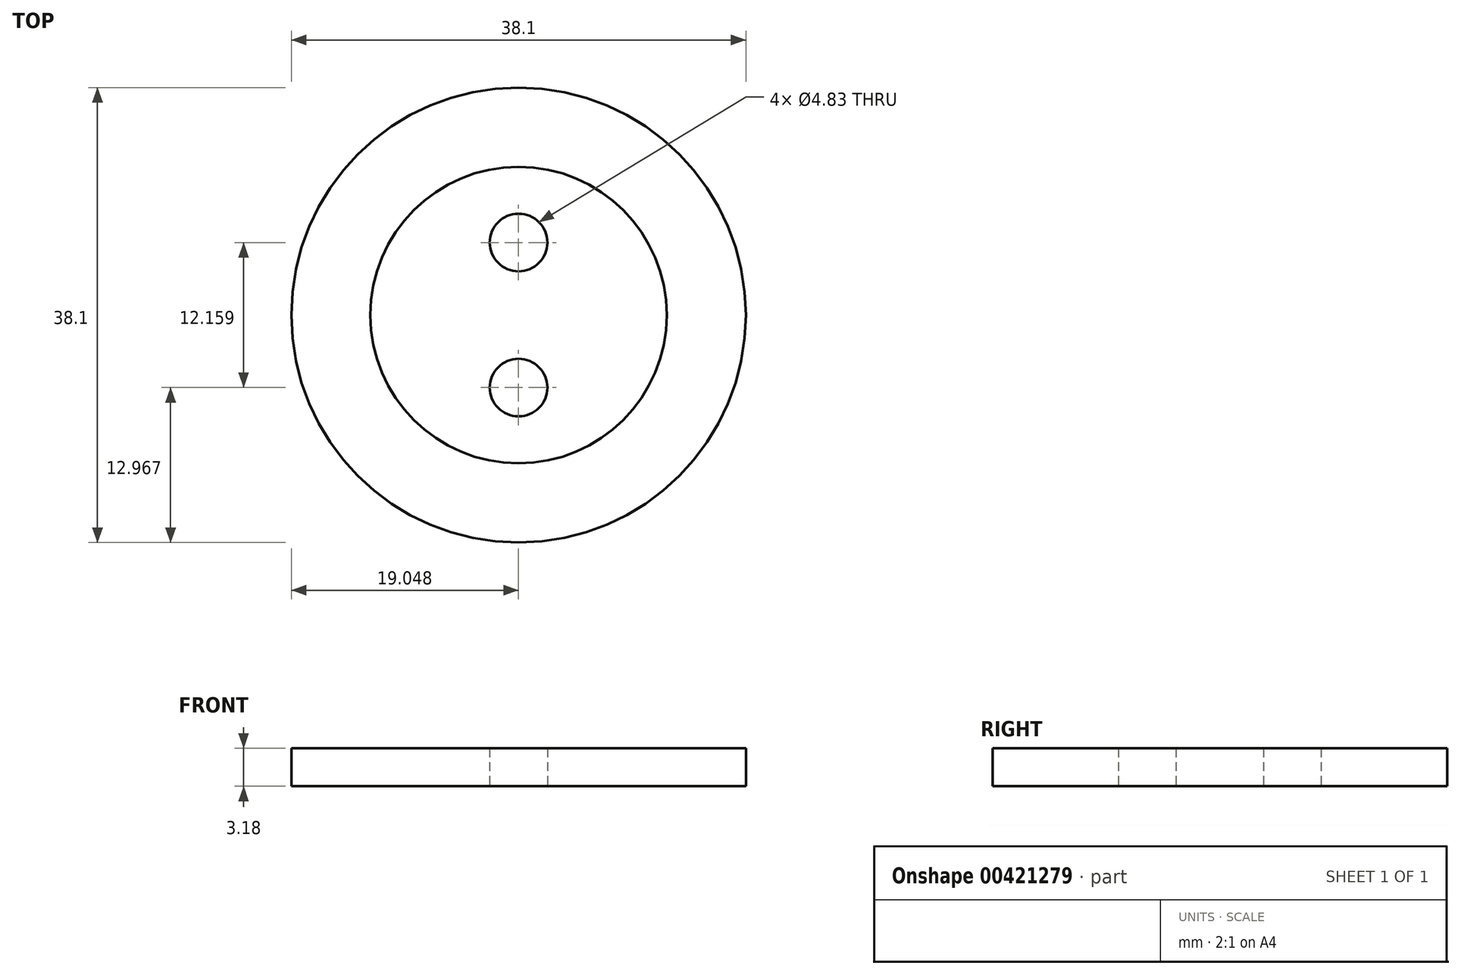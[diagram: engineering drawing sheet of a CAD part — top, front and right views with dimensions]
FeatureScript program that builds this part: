
annotation { "Feature Type Name" : "Feature", "Feature Type Description" : "" }
export const myFeature = defineFeature(function(context is Context, id is Id, definition is map)
    precondition{}
    {
        {
            assignVariable(context, id + "F0", {"name" : "flange_thickness", "anyValue" : 3.17 * mm});
        }
        {
            var Q0;
            Q0=qCreatedBy(makeId("Top.planeOp"),FACE);
            var sketch = newSketch(context, id + "F1", { "sketchPlane" : qUnion([Q0])});
            skCircle(sketch, "E0", {"center": v(-45.4, 36.92) * mm, "radius": 19.05 * mm});
            skCircle(sketch, "E1", {"center": v(-45.4, 36.92) * mm, "radius": 6.08 * mm, "construction": true});
            skCircle(sketch, "E2", {"center": v(-45.4, 43) * mm, "radius": 2.41 * mm});
            skCircle(sketch, "E3", {"center": v(-45.4, 30.84) * mm, "radius": 2.41 * mm});
            skSolve(sketch);
        }
        {
            var Q0;
            Q0=makeQuery(id+"F1.imprint","IMPRINT",FACE,{"disambiguationData":[TD([[makeQuery(id+"F1.imprint","IMPRINT",EDGE,{"derivedFrom":sQuery(id+"F1.wireOp",EDGE,"E0")}),1.0]])]});
            extrude(context, id + "F2", {"entities" : qUnion([Q0]), "depth" : getVariable(context, 'flange_thickness')});
        }
        {
            var Q0;
            Q0=makeQuery(id+"F2.opExtrude","CAP_FACE",FACE,{"disambiguationData":[OSD([sQuery(id+"F1.wireOp",EDGE,"E0"),sQuery(id+"F1.wireOp",EDGE,"E2"),sQuery(id+"F1.wireOp",EDGE,"E3")])],"isStart":false});
            var sketch = newSketch(context, id + "F3", { "sketchPlane" : qUnion([Q0])});
            skCircle(sketch, "E4.0.0", {"center": v(-45.4, 36.92) * mm, "radius": 19.05 * mm});
            skCircle(sketch, "E5", {"center": v(-45.4, 36.92) * mm, "radius": 12.42 * mm});
            skCircle(sketch, "E6.0", {"center": v(-45.4, 43) * mm, "radius": 2.41 * mm});
            skCircle(sketch, "E7.0", {"center": v(-45.4, 30.84) * mm, "radius": 2.41 * mm});
            skSolve(sketch);
        }
        {
            var Q0;
            Q0=makeQuery(id+"F3.imprint","IMPRINT",FACE,{"disambiguationData":[TD([[makeQuery(id+"F3.imprint","IMPRINT",EDGE,{"derivedFrom":sQuery(id+"F3.wireOp",EDGE,"E5")}),1.0]])]});
            extrude(context, id + "F4", {"entities" : qUnion([Q0]), "depth" : 1 / 101.6 * mm});
        }
    });
